# Revit family: Gira_015230
name_source: partatom
category: Electrical Fixtures
revit_build: Autodesk Revit 2017 (Build: 20160225_1515(x64)
units: mm (PartAtom-declared; Revit-internal decimal feet)

## family parameters
Cut with Voids When Loaded = No
Host = Face
Maintain Annotation Orientation = Yes
Part Type = Normal
Room Calculation Point = No
Round Connector Dimension = Use Diameter
Shared = No

## types (1)
- Rocker btn NO con. s.sig. in.sp. WP surface-mounted grey
    Assembly arrangement = Basic element with complete housing
    Available = No
    BIM (1) = https://media.stage.bim.site und Tasten.rfa?public/gira/36a6b08/IP44_Komplettgerät_Schalten und Tasten.rfa
    Category = Push-switch button
    Colour = Grey
    Data sheet (1) = https://katalog.gira.de
    Default Elevation = 1219 mm
    Description = Rock.btn NO con.s.sig.in.sp. WP SM GY,Rocker Button 10 AX 250 V~ with inscription space,NO contact, 1-pole with sep. signal contact,grey,Notes :,- Can also be connected with illumination.
    GTIN = 4010337152309
    HAN = 015230
    Halogen free = No
    HeinzeBIM = https://bimportal.heinze.de
    Imprint = None
    Label space/information surface = No
    Manufacturer = Gira
    Manufacturer URL = https://www.gira.de
    Material = Other
    Material quality = Other
    Method of operation = Rocker
    Model = Single push button
    Mounting method = Surface mounted (plaster)
    Name = Rocker btn NO con. s.sig. in.sp. WP surface-mounted grey
    Nominal voltage = 250
    Number of rockers = 1
    Rated current = 10
    Suitable for degree of protection (IP) = IP44
    Surface protection = Other
    Transparent = No
    URL = http://katalog.gira.de
    With lighting = No

## geometry (parser evidence)
native form markers: Sweep x1
no freeform markers — native parametric forms only
